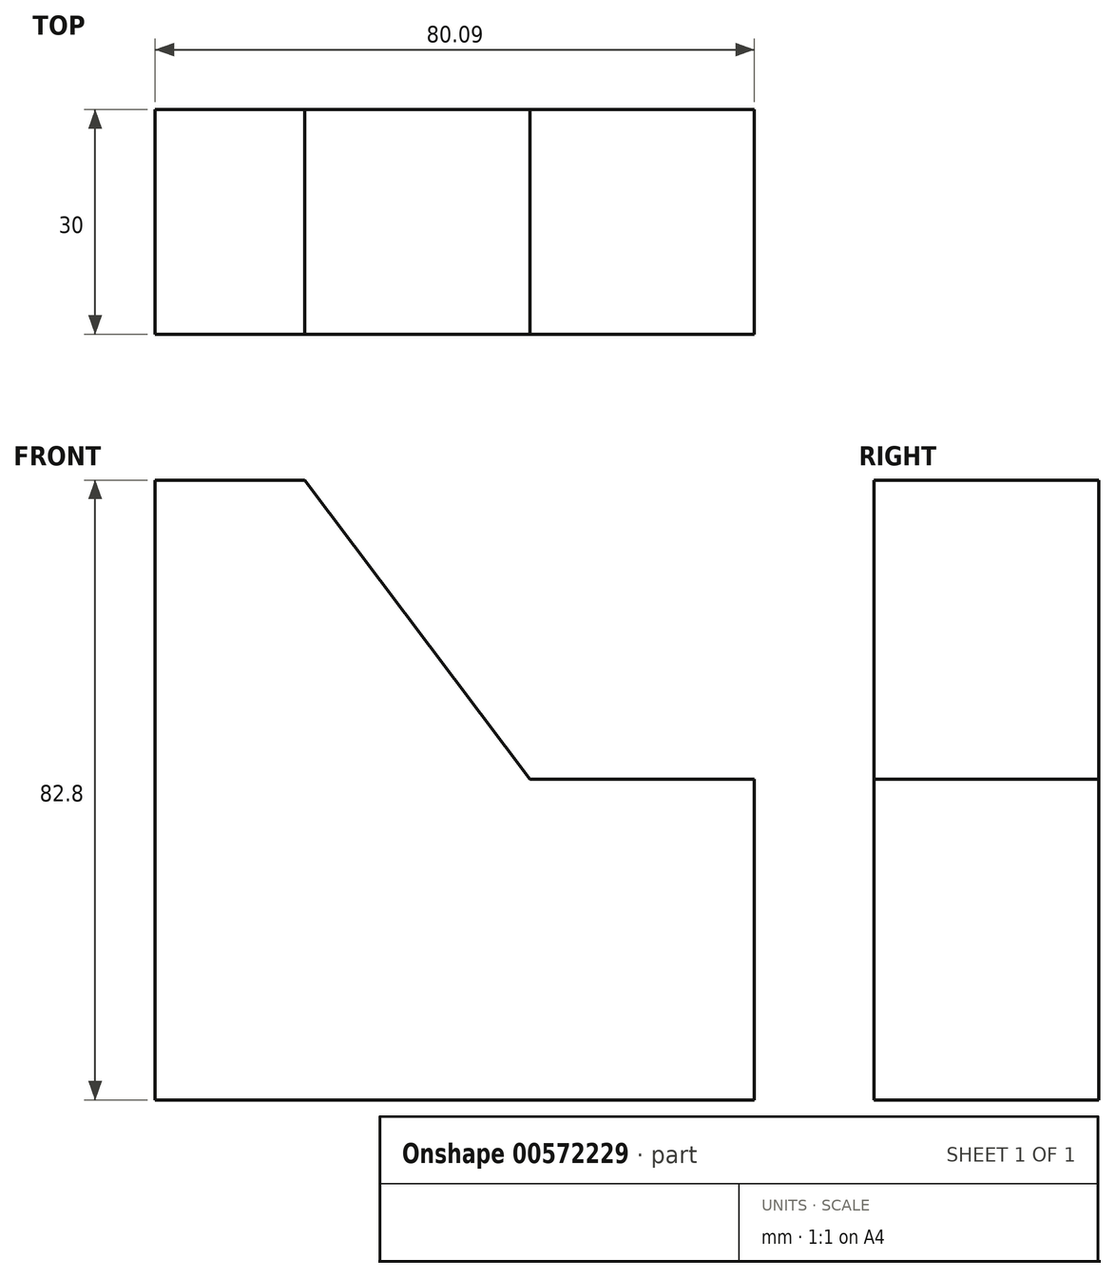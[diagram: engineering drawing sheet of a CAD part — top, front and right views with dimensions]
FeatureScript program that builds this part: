
annotation { "Feature Type Name" : "Feature", "Feature Type Description" : "" }
export const myFeature = defineFeature(function(context is Context, id is Id, definition is map)
    precondition{}
    {
        {
            var Q0;
            Q0=qCreatedBy(makeId("Front.planeOp"),FACE);
            var sketch = newSketch(context, id + "F0", { "sketchPlane" : qUnion([Q0])});
            skLineSegment(sketch, "E0", {"start": v(-55.08, 49.9) * mm, "end": v(-55.08, -32.9) * mm});
            skLineSegment(sketch, "E1", {"start": v(-55.08, -32.9) * mm, "end": v(25, -32.9) * mm});
            skLineSegment(sketch, "E2", {"start": v(25, -32.9) * mm, "end": v(25, 9.97) * mm});
            skLineSegment(sketch, "E3", {"start": v(25, 9.97) * mm, "end": v(-5, 9.97) * mm});
            skLineSegment(sketch, "E4", {"start": v(-5, 9.97) * mm, "end": v(-35.08, 49.9) * mm});
            skLineSegment(sketch, "E5", {"start": v(-35.08, 49.9) * mm, "end": v(-55.08, 49.9) * mm});
            skSolve(sketch);
        }
        {
            var Q0;
            Q0 = qSketchRegion(id + "F0", true);
            extrude(context, id + "F1", {"entities" : qUnion([Q0]), "depth" : 30 * mm, "offsetDistance" : 25 * mm});
        }
    });
